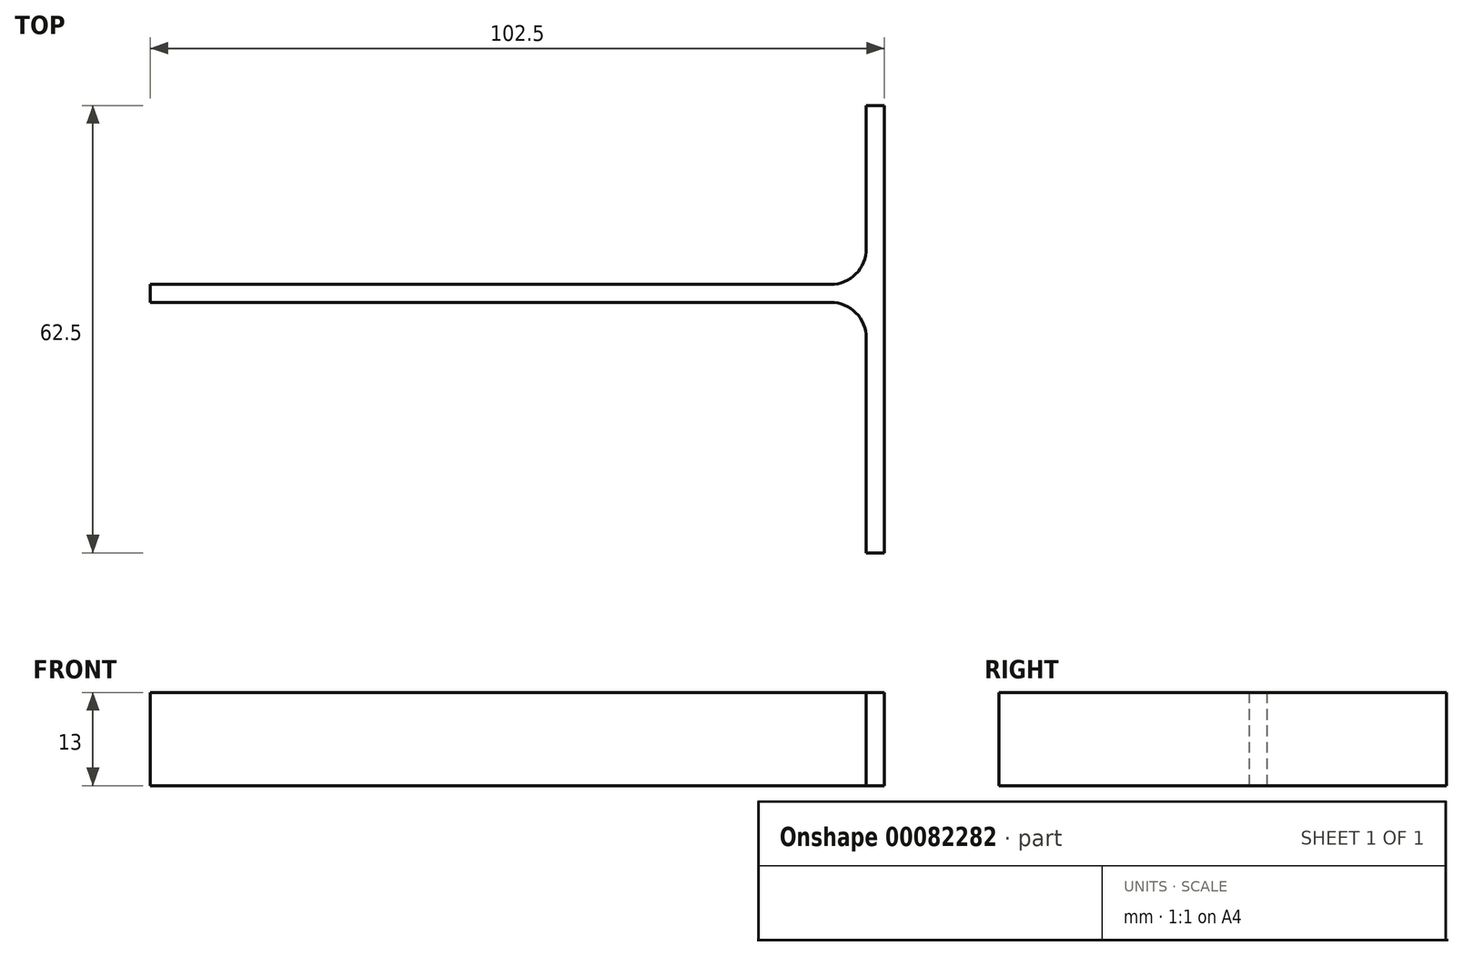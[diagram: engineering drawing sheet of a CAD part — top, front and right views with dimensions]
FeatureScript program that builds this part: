
annotation { "Feature Type Name" : "Feature", "Feature Type Description" : "" }
export const myFeature = defineFeature(function(context is Context, id is Id, definition is map)
    precondition{}
    {
        {
            var Q0;
            Q0=qCreatedBy(makeId("Top.planeOp"),FACE);
            var sketch = newSketch(context, id + "F0", { "sketchPlane" : qUnion([Q0])});
            skLineSegment(sketch, "E0", {"start": v(-62.4, 0) * mm, "end": v(37.6, 0) * mm});
            skLineSegment(sketch, "E1", {"start": v(37.6, 0) * mm, "end": v(37.6, -35) * mm});
            skLineSegment(sketch, "E2", {"start": v(40.1, -35) * mm, "end": v(40.1, 27.5) * mm});
            skLineSegment(sketch, "E3", {"start": v(37.6, 27.5) * mm, "end": v(37.6, 2.5) * mm});
            skLineSegment(sketch, "E4", {"start": v(37.6, 2.5) * mm, "end": v(-62.4, 2.5) * mm});
            skLineSegment(sketch, "E5", {"start": v(-62.4, 2.5) * mm, "end": v(-62.4, 0) * mm});
            skLineSegment(sketch, "E6", {"start": v(40.1, -35) * mm, "end": v(37.6, -35) * mm});
            skLineSegment(sketch, "E7", {"start": v(40.1, 27.5) * mm, "end": v(37.6, 27.5) * mm});
            skPoint(sketch, "E8.orphan", {"position": v(37.6, 29.05) * mm});
            skSolve(sketch);
        }
        {
            var Q0;
            Q0=makeQuery(id+"F0.imprint","IMPRINT",FACE,{"disambiguationData":[TD([[makeQuery(id+"F0.imprint","IMPRINT",EDGE,{"derivedFrom":sQuery(id+"F0.wireOp",EDGE,"E0")}),1.0]])]});
            extrude(context, id + "F1", {"entities" : qUnion([Q0]), "oppositeDirection" : true, "depth" : 13 * mm, "offsetDistance" : 25 * mm});
        }
        {
            var Q0;
            Q0=makeQuery(id+"F1.opExtrude","SWEPT_EDGE",EDGE,{"disambiguationData":[OSD([sQuery(id+"F0.wireOp",EDGE,"E0"),sQuery(id+"F0.wireOp",EDGE,"E1")])]});
            var Q1;
            Q1=makeQuery(id+"F1.opExtrude","SWEPT_EDGE",EDGE,{"disambiguationData":[OSD([sQuery(id+"F0.wireOp",EDGE,"E3"),sQuery(id+"F0.wireOp",EDGE,"E4")])]});
            fillet(context, id + "F2", {"entities" : qUnion([Q0, Q1]), "tangentPropagation" : true, "radius" : 5 * mm, "defaultsChanged" : false, "vertexSettings" : [], "allowEdgeOverflow" : false});
        }
    });
